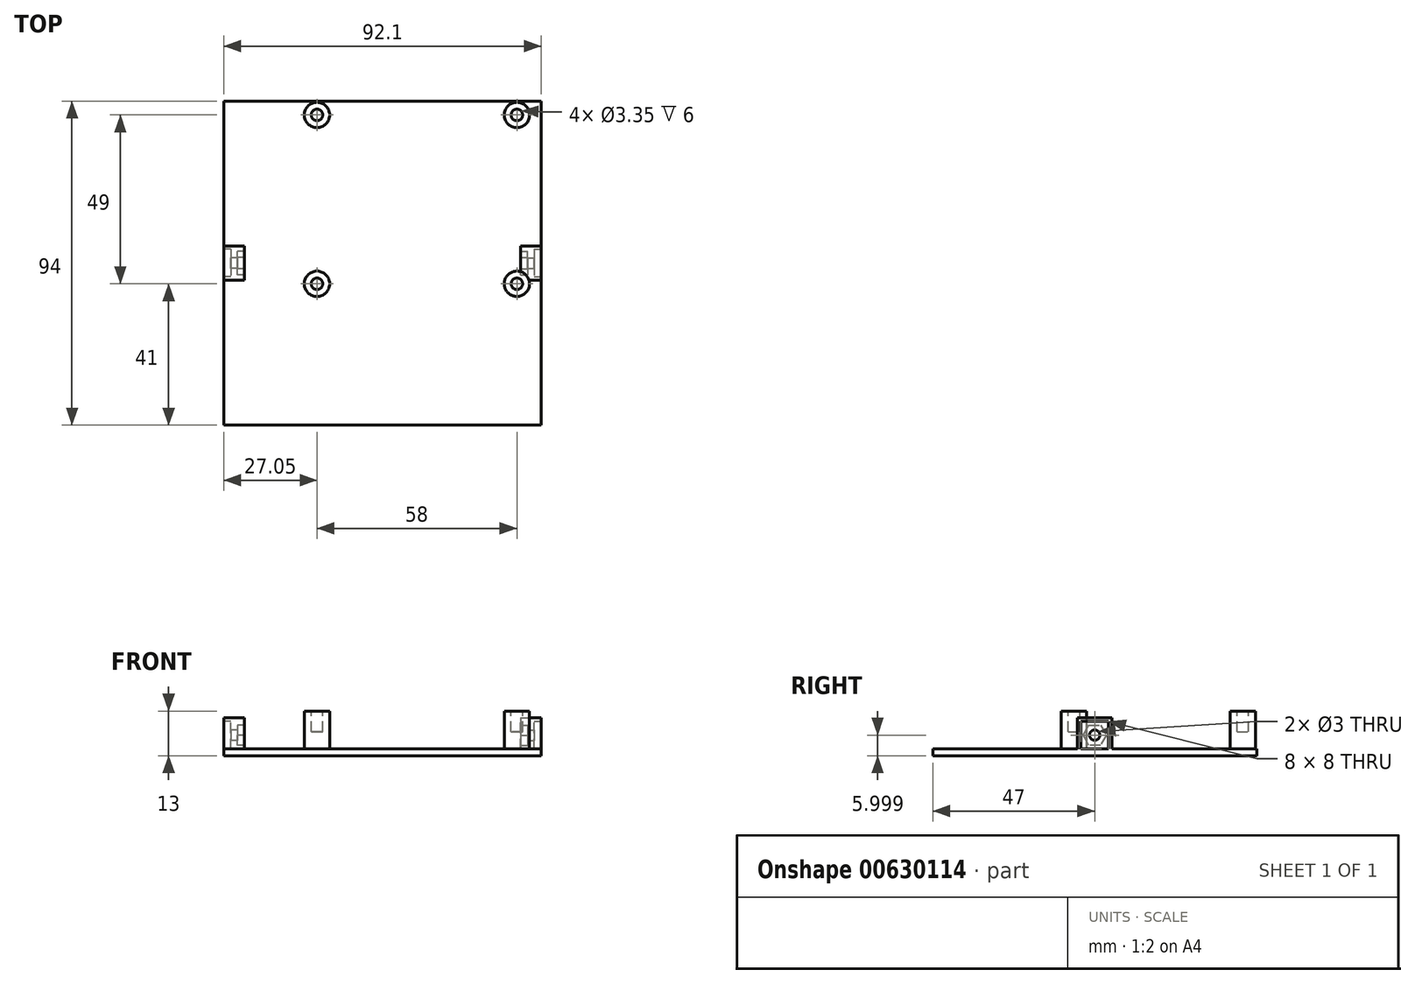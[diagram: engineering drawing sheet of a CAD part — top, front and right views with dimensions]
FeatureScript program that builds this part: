
annotation { "Feature Type Name" : "Feature", "Feature Type Description" : "" }
export const myFeature = defineFeature(function(context is Context, id is Id, definition is map)
    precondition{}
    {
        {
            var Q0;
            Q0=qCreatedBy(makeId("Right.planeOp"),FACE);
            var sketch = newSketch(context, id + "F0", { "sketchPlane" : qUnion([Q0])});
            skLineSegment(sketch, "E0.7", {"start": v(47, 6.17) * mm, "end": v(-47, 6.17) * mm});
            skLineSegment(sketch, "E1", {"start": v(47, 4.17) * mm, "end": v(-47, 4.17) * mm});
            skLineSegment(sketch, "E2", {"start": v(47, 6.17) * mm, "end": v(47, 4.17) * mm});
            skLineSegment(sketch, "E3", {"start": v(-47, 6.17) * mm, "end": v(-47, 4.17) * mm});
            skSolve(sketch);
        }
        {
            var Q0;
            Q0 = qSketchRegion(id + "F0", true);
            extrude(context, id + "F1", {"entities" : qUnion([Q0]), "depth" : 92.1 * mm, "offsetDistance" : 25 * mm, "symmetric" : true});
        }
        {
            var Q0;
            Q0=makeQuery(id+"F1.opExtrude","CAP_FACE",FACE,{"disambiguationData":[OSD([sQuery(id+"F0.wireOp",EDGE,"E0.7"),sQuery(id+"F0.wireOp",EDGE,"E1"),sQuery(id+"F0.wireOp",EDGE,"E2"),sQuery(id+"F0.wireOp",EDGE,"E3")])],"isStart":true});
            var sketch = newSketch(context, id + "F2", { "sketchPlane" : qUnion([Q0])});
            skPoint(sketch, "E4", {"position": v(0, 4.17) * mm});
            skLineSegment(sketch, "E5", {"start": v(0, 4.17) * mm, "end": v(0, 7.17) * mm, "construction": true});
            skLineSegment(sketch, "E6", {"start": v(0, 7.17) * mm, "end": v(0, 13.17) * mm, "construction": true});
            skPoint(sketch, "E7", {"position": v(0, 10.17) * mm});
            skCircle(sketch, "E8", {"center": v(0, 10.17) * mm, "radius": 1.5 * mm});
            skCircle(sketch, "E9", {"center": v(0, 10.17) * mm, "radius": 2.75 * mm, "construction": true});
            skLineSegment(sketch, "E10.bottom", {"start": v(-3, 7.17) * mm, "end": v(-3, 13.17) * mm, "construction": true});
            skLineSegment(sketch, "E10.top", {"start": v(3, 7.17) * mm, "end": v(3, 13.17) * mm, "construction": true});
            skLineSegment(sketch, "E10.left", {"start": v(-3, 7.17) * mm, "end": v(3, 7.17) * mm, "construction": true});
            skLineSegment(sketch, "E10.right", {"start": v(-3, 13.17) * mm, "end": v(3, 13.17) * mm, "construction": true});
            skLineSegment(sketch, "E11.bottom", {"start": v(-4, 6.17) * mm, "end": v(-4, 14.17) * mm});
            skLineSegment(sketch, "E11.top", {"start": v(4, 6.17) * mm, "end": v(4, 14.17) * mm});
            skLineSegment(sketch, "E11.left", {"start": v(-4, 6.17) * mm, "end": v(4, 6.17) * mm});
            skLineSegment(sketch, "E11.right", {"start": v(-4, 14.17) * mm, "end": v(4, 14.17) * mm});
            skLineSegment(sketch, "E12.bottom", {"start": v(-5, 5.17) * mm, "end": v(-5, 15.17) * mm});
            skLineSegment(sketch, "E12.top", {"start": v(5, 5.17) * mm, "end": v(5, 15.17) * mm});
            skLineSegment(sketch, "E12.left", {"start": v(-5, 5.17) * mm, "end": v(5, 5.17) * mm, "construction": true});
            skLineSegment(sketch, "E12.right", {"start": v(-5, 15.17) * mm, "end": v(5, 15.17) * mm});
            skSolve(sketch);
        }
        {
            var Q0;
            {var subQ6=sQuery(id+"F2.wireOp",EDGE,"E11.bottom");Q0=makeQuery(id+"F2.imprint","IMPRINT",FACE,{"disambiguationData":[TD([[makeQuery(id+"F2.imprint","IMPRINT",EDGE,{"derivedFrom":subQ6}),1.0]])]});}
            var Q1;
            Q1=makeQuery(id+"F2.imprint","IMPRINT",FACE,{"disambiguationData":[TD([[makeQuery(id+"F2.imprint","IMPRINT",EDGE,{"derivedFrom":sQuery(id+"F2.wireOp",EDGE,"E8")}),-1.0]])]});
            extrude(context, id + "F3", {"entities" : qUnion([Q0, Q1]), "operationType" : NewBodyOperationType.ADD, "oppositeDirection" : true, "depth" : 4 * mm, "offsetDistance" : 25 * mm});
        }
        {
            var Q0;
            Q0=makeQuery(id+"F2.imprint","IMPRINT",FACE,{"disambiguationData":[TD([[makeQuery(id+"F2.imprint","IMPRINT",EDGE,{"derivedFrom":sQuery(id+"F2.wireOp",EDGE,"E8")}),-1.0]])]});
            extrude(context, id + "F4", {"entities" : qUnion([Q0]), "operationType" : NewBodyOperationType.REMOVE, "oppositeDirection" : true, "depth" : 2 * mm, "offsetDistance" : 25 * mm});
        }
        {
            var Q0;
            Q0=makeQuery(id+"F3.opExtrude","CAP_FACE",FACE,{"disambiguationData":[OSD([sQuery(id+"F0.wireOp",EDGE,"E0.7"),sQuery(id+"F2.wireOp",EDGE,"E8"),sQuery(id+"F2.wireOp",EDGE,"E11.left"),sQuery(id+"F2.wireOp",EDGE,"E12.bottom"),sQuery(id+"F2.wireOp",EDGE,"E12.top"),sQuery(id+"F2.wireOp",EDGE,"E12.right")])],"isStart":false});
            var sketch = newSketch(context, id + "F5", { "sketchPlane" : qUnion([Q0])});
            skCircle(sketch, "E13.cCircle", {"center": v(0, 10.17) * mm, "radius": 2.92 * mm, "construction": true});
            skLineSegment(sketch, "E13.0", {"start": v(3.38, 10.17) * mm, "end": v(1.69, 7.25) * mm});
            skLineSegment(sketch, "E13.1", {"start": v(1.69, 7.25) * mm, "end": v(-1.69, 7.25) * mm});
            skLineSegment(sketch, "E13.2", {"start": v(-1.69, 7.25) * mm, "end": v(-3.37, 10.17) * mm});
            skLineSegment(sketch, "E13.3", {"start": v(-3.37, 10.17) * mm, "end": v(-1.69, 13.1) * mm});
            skLineSegment(sketch, "E13.4", {"start": v(-1.69, 13.1) * mm, "end": v(1.69, 13.1) * mm});
            skLineSegment(sketch, "E13.5", {"start": v(1.69, 13.1) * mm, "end": v(3.38, 10.17) * mm});
            skPoint(sketch, "E13.0.midPoint", {"position": v(2.53, 8.7) * mm});
            skLineSegment(sketch, "E14.bottom", {"start": v(-5, 15.17) * mm, "end": v(5, 15.17) * mm});
            skLineSegment(sketch, "E14.top", {"start": v(-5, 6.17) * mm, "end": v(5, 6.17) * mm});
            skLineSegment(sketch, "E14.left", {"start": v(-5, 15.17) * mm, "end": v(-5, 6.17) * mm});
            skLineSegment(sketch, "E14.right", {"start": v(5, 15.17) * mm, "end": v(5, 6.17) * mm});
            skSolve(sketch);
        }
        {
            var Q0;
            Q0=makeQuery(id+"F5.imprint","IMPRINT",FACE,{"disambiguationData":[TD([[makeQuery(id+"F5.imprint","IMPRINT",EDGE,{"derivedFrom":sQuery(id+"F5.wireOp",EDGE,"E13.0")}),1.0]])]});
            extrude(context, id + "F6", {"entities" : qUnion([Q0]), "operationType" : NewBodyOperationType.ADD, "depth" : 2 * mm, "offsetDistance" : 25 * mm});
        }
        {
            var Q0;
            Q0=makeQuery(id+"F1.opExtrude","SWEPT_BODY",BODY,{"disambiguationData":[OSD([sQuery(id+"F0.wireOp",EDGE,"E0.7"),sQuery(id+"F0.wireOp",EDGE,"E1"),sQuery(id+"F0.wireOp",EDGE,"E2"),sQuery(id+"F0.wireOp",EDGE,"E3")])]});
            var Q1;
            Q1=qCreatedBy(makeId("Right.planeOp"),FACE);
            mirror(context, id + "F7", {"entities" : qUnion([Q0]), "mirrorPlane" : qUnion([Q1])});
        }
        {
            var Q0;
            {var subQ10=sQuery(id+"F0.wireOp",EDGE,"E2");var subQ12=sQuery(id+"F0.wireOp",EDGE,"E0.7");Q0=makeQuery(id+"FgA4i82gOfAXOqg_2.opBoolean","SPLIT",FACE,{"disambiguationData":[TD([makeQuery(id+"F1.opExtrude","SWEPT_FACE",FACE,{"disambiguationData":[OSD([subQ10])]})])],"derivedFrom":makeQuery(id+"F1.opExtrude","SWEPT_FACE",FACE,{"disambiguationData":[OSD([subQ12])]})});}
            var sketch = newSketch(context, id + "F8", { "sketchPlane" : qUnion([Q0])});
            skLineSegment(sketch, "E15.bottom", {"start": v(42.5, 46.5) * mm, "end": v(-42.5, 46.5) * mm});
            skLineSegment(sketch, "E15.top", {"start": v(42.5, -9.5) * mm, "end": v(-42.5, -9.5) * mm});
            skLineSegment(sketch, "E15.left", {"start": v(42.5, 46.5) * mm, "end": v(42.5, -9.5) * mm});
            skLineSegment(sketch, "E15.right", {"start": v(-42.5, 46.5) * mm, "end": v(-42.5, -9.5) * mm});
            skCircle(sketch, "E16", {"center": v(39, -6) * mm, "radius": 1.38 * mm});
            skCircle(sketch, "E17", {"center": v(-19, -6) * mm, "radius": 1.38 * mm});
            skCircle(sketch, "E18", {"center": v(-19, 43) * mm, "radius": 1.38 * mm});
            skCircle(sketch, "E19", {"center": v(39, 43) * mm, "radius": 1.37 * mm});
            skLineSegment(sketch, "E20.bottom", {"start": v(35, -8.5) * mm, "end": v(-15, -8.5) * mm, "construction": true});
            skLineSegment(sketch, "E20.top", {"start": v(35, -3.5) * mm, "end": v(-15, -3.5) * mm, "construction": true});
            skLineSegment(sketch, "E20.left", {"start": v(35, -8.5) * mm, "end": v(35, -3.5) * mm, "construction": true});
            skLineSegment(sketch, "E20.right", {"start": v(-15, -8.5) * mm, "end": v(-15, -3.5) * mm, "construction": true});
            skLineSegment(sketch, "E21", {"start": v(10, -8.5) * mm, "end": v(10, -3.5) * mm, "construction": true});
            skLineSegment(sketch, "E22", {"start": v(35, -6) * mm, "end": v(-15, -6) * mm, "construction": true});
            skLineSegment(sketch, "E23.bottom", {"start": v(34.05, -7.55) * mm, "end": v(33.45, -7.55) * mm});
            skLineSegment(sketch, "E23.top", {"start": v(34.05, -6.95) * mm, "end": v(33.45, -6.95) * mm});
            skLineSegment(sketch, "E23.left", {"start": v(34.05, -7.55) * mm, "end": v(34.05, -6.95) * mm});
            skLineSegment(sketch, "E23.right", {"start": v(33.45, -7.55) * mm, "end": v(33.45, -6.95) * mm});
            skLineSegment(sketch, "E24", {"start": v(32.5, -8.5) * mm, "end": v(32.5, -3.5) * mm, "construction": true});
            skLineSegment(sketch, "E25.1.0.0", {"start": v(31.55, -6.95) * mm, "end": v(30.95, -6.95) * mm});
            skLineSegment(sketch, "E25.1.0.1", {"start": v(31.55, -7.55) * mm, "end": v(30.95, -7.55) * mm});
            skLineSegment(sketch, "E25.1.0.2", {"start": v(30.95, -7.55) * mm, "end": v(30.95, -6.95) * mm});
            skLineSegment(sketch, "E25.1.0.3", {"start": v(31.55, -7.55) * mm, "end": v(31.55, -6.95) * mm});
            skLineSegment(sketch, "E25.2.0.0", {"start": v(29.05, -6.95) * mm, "end": v(28.45, -6.95) * mm});
            skLineSegment(sketch, "E25.2.0.1", {"start": v(29.05, -7.55) * mm, "end": v(28.45, -7.55) * mm});
            skLineSegment(sketch, "E25.2.0.2", {"start": v(28.45, -7.55) * mm, "end": v(28.45, -6.95) * mm});
            skLineSegment(sketch, "E25.2.0.3", {"start": v(29.05, -7.55) * mm, "end": v(29.05, -6.95) * mm});
            skLineSegment(sketch, "E25.3.0.0", {"start": v(26.55, -6.95) * mm, "end": v(25.95, -6.95) * mm});
            skLineSegment(sketch, "E25.3.0.1", {"start": v(26.55, -7.55) * mm, "end": v(25.95, -7.55) * mm});
            skLineSegment(sketch, "E25.3.0.2", {"start": v(25.95, -7.55) * mm, "end": v(25.95, -6.95) * mm});
            skLineSegment(sketch, "E25.3.0.3", {"start": v(26.55, -7.55) * mm, "end": v(26.55, -6.95) * mm});
            skLineSegment(sketch, "E25.4.0.0", {"start": v(24.05, -6.95) * mm, "end": v(23.45, -6.95) * mm});
            skLineSegment(sketch, "E25.4.0.1", {"start": v(24.05, -7.55) * mm, "end": v(23.45, -7.55) * mm});
            skLineSegment(sketch, "E25.4.0.2", {"start": v(23.45, -7.55) * mm, "end": v(23.45, -6.95) * mm});
            skLineSegment(sketch, "E25.4.0.3", {"start": v(24.05, -7.55) * mm, "end": v(24.05, -6.95) * mm});
            skLineSegment(sketch, "E25.5.0.0", {"start": v(21.55, -6.95) * mm, "end": v(20.95, -6.95) * mm});
            skLineSegment(sketch, "E25.5.0.1", {"start": v(21.55, -7.55) * mm, "end": v(20.95, -7.55) * mm});
            skLineSegment(sketch, "E25.5.0.2", {"start": v(20.95, -7.55) * mm, "end": v(20.95, -6.95) * mm});
            skLineSegment(sketch, "E25.5.0.3", {"start": v(21.55, -7.55) * mm, "end": v(21.55, -6.95) * mm});
            skLineSegment(sketch, "E25.6.0.0", {"start": v(19.05, -6.95) * mm, "end": v(18.45, -6.95) * mm});
            skLineSegment(sketch, "E25.6.0.1", {"start": v(19.05, -7.55) * mm, "end": v(18.45, -7.55) * mm});
            skLineSegment(sketch, "E25.6.0.2", {"start": v(18.45, -7.55) * mm, "end": v(18.45, -6.95) * mm});
            skLineSegment(sketch, "E25.6.0.3", {"start": v(19.05, -7.55) * mm, "end": v(19.05, -6.95) * mm});
            skLineSegment(sketch, "E25.7.0.0", {"start": v(16.55, -6.95) * mm, "end": v(15.95, -6.95) * mm});
            skLineSegment(sketch, "E25.7.0.1", {"start": v(16.55, -7.55) * mm, "end": v(15.95, -7.55) * mm});
            skLineSegment(sketch, "E25.7.0.2", {"start": v(15.95, -7.55) * mm, "end": v(15.95, -6.95) * mm});
            skLineSegment(sketch, "E25.7.0.3", {"start": v(16.55, -7.55) * mm, "end": v(16.55, -6.95) * mm});
            skLineSegment(sketch, "E25.8.0.0", {"start": v(14.05, -6.95) * mm, "end": v(13.45, -6.95) * mm});
            skLineSegment(sketch, "E25.8.0.1", {"start": v(14.05, -7.55) * mm, "end": v(13.45, -7.55) * mm});
            skLineSegment(sketch, "E25.8.0.2", {"start": v(13.45, -7.55) * mm, "end": v(13.45, -6.95) * mm});
            skLineSegment(sketch, "E25.8.0.3", {"start": v(14.05, -7.55) * mm, "end": v(14.05, -6.95) * mm});
            skLineSegment(sketch, "E25.9.0.0", {"start": v(11.55, -6.95) * mm, "end": v(10.95, -6.95) * mm});
            skLineSegment(sketch, "E25.9.0.1", {"start": v(11.55, -7.55) * mm, "end": v(10.95, -7.55) * mm});
            skLineSegment(sketch, "E25.9.0.2", {"start": v(10.95, -7.55) * mm, "end": v(10.95, -6.95) * mm});
            skLineSegment(sketch, "E25.9.0.3", {"start": v(11.55, -7.55) * mm, "end": v(11.55, -6.95) * mm});
            skLineSegment(sketch, "E25.direction1", {"start": v(34.05, -6.95) * mm, "end": v(31.55, -6.95) * mm, "construction": true});
            skLineSegment(sketch, "E26.MirrorCS", {"start": v(14.05, -5.05) * mm, "end": v(13.45, -5.05) * mm});
            skLineSegment(sketch, "E27.MirrorCS", {"start": v(14.05, -4.45) * mm, "end": v(13.45, -4.45) * mm});
            skLineSegment(sketch, "E28.MirrorCS", {"start": v(11.55, -4.45) * mm, "end": v(10.95, -4.45) * mm});
            skLineSegment(sketch, "E29.MirrorCS", {"start": v(31.55, -4.45) * mm, "end": v(30.95, -4.45) * mm});
            skLineSegment(sketch, "E30.MirrorCS", {"start": v(31.55, -5.05) * mm, "end": v(30.95, -5.05) * mm});
            skLineSegment(sketch, "E31.MirrorCS", {"start": v(11.55, -5.05) * mm, "end": v(10.95, -5.05) * mm});
            skLineSegment(sketch, "E32.MirrorCS", {"start": v(34.05, -4.45) * mm, "end": v(33.45, -4.45) * mm});
            skLineSegment(sketch, "E33.MirrorCS", {"start": v(34.05, -5.05) * mm, "end": v(33.45, -5.05) * mm});
            skLineSegment(sketch, "E34.MirrorCS", {"start": v(33.45, -4.45) * mm, "end": v(33.45, -5.05) * mm});
            skLineSegment(sketch, "E35.MirrorCS", {"start": v(24.05, -4.45) * mm, "end": v(24.05, -5.05) * mm});
            skLineSegment(sketch, "E36.MirrorCS", {"start": v(14.05, -4.45) * mm, "end": v(14.05, -5.05) * mm});
            skLineSegment(sketch, "E37.MirrorCS", {"start": v(21.55, -4.45) * mm, "end": v(21.55, -5.05) * mm});
            skLineSegment(sketch, "E38.MirrorCS", {"start": v(24.05, -5.05) * mm, "end": v(23.45, -5.05) * mm});
            skLineSegment(sketch, "E39.MirrorCS", {"start": v(11.55, -4.45) * mm, "end": v(11.55, -5.05) * mm});
            skLineSegment(sketch, "E40.MirrorCS", {"start": v(31.55, -4.45) * mm, "end": v(31.55, -5.05) * mm});
            skLineSegment(sketch, "E41.MirrorCS", {"start": v(28.45, -4.45) * mm, "end": v(28.45, -5.05) * mm});
            skLineSegment(sketch, "E42.MirrorCS", {"start": v(18.45, -4.45) * mm, "end": v(18.45, -5.05) * mm});
            skLineSegment(sketch, "E43.MirrorCS", {"start": v(23.45, -4.45) * mm, "end": v(23.45, -5.05) * mm});
            skLineSegment(sketch, "E44.MirrorCS", {"start": v(13.45, -4.45) * mm, "end": v(13.45, -5.05) * mm});
            skLineSegment(sketch, "E45.MirrorCS", {"start": v(20.95, -4.45) * mm, "end": v(20.95, -5.05) * mm});
            skLineSegment(sketch, "E46.MirrorCS", {"start": v(26.55, -4.45) * mm, "end": v(26.55, -5.05) * mm});
            skLineSegment(sketch, "E47.MirrorCS", {"start": v(10.95, -4.45) * mm, "end": v(10.95, -5.05) * mm});
            skLineSegment(sketch, "E48.MirrorCS", {"start": v(16.55, -4.45) * mm, "end": v(16.55, -5.05) * mm});
            skLineSegment(sketch, "E49.MirrorCS", {"start": v(30.95, -4.45) * mm, "end": v(30.95, -5.05) * mm});
            skLineSegment(sketch, "E50.MirrorCS", {"start": v(29.05, -4.45) * mm, "end": v(28.45, -4.45) * mm});
            skLineSegment(sketch, "E51.MirrorCS", {"start": v(19.05, -4.45) * mm, "end": v(18.45, -4.45) * mm});
            skLineSegment(sketch, "E52.MirrorCS", {"start": v(26.55, -4.45) * mm, "end": v(25.95, -4.45) * mm});
            skLineSegment(sketch, "E53.MirrorCS", {"start": v(16.55, -4.45) * mm, "end": v(15.95, -4.45) * mm});
            skLineSegment(sketch, "E54.MirrorCS", {"start": v(24.05, -4.45) * mm, "end": v(23.45, -4.45) * mm});
            skLineSegment(sketch, "E55.MirrorCS", {"start": v(34.05, -4.45) * mm, "end": v(34.05, -5.05) * mm});
            skLineSegment(sketch, "E56.MirrorCS", {"start": v(21.55, -4.45) * mm, "end": v(20.95, -4.45) * mm});
            skLineSegment(sketch, "E57.MirrorCS", {"start": v(25.95, -4.45) * mm, "end": v(25.95, -5.05) * mm});
            skLineSegment(sketch, "E58.MirrorCS", {"start": v(15.95, -4.45) * mm, "end": v(15.95, -5.05) * mm});
            skLineSegment(sketch, "E59.MirrorCS", {"start": v(29.05, -5.05) * mm, "end": v(28.45, -5.05) * mm});
            skLineSegment(sketch, "E60.MirrorCS", {"start": v(19.05, -5.05) * mm, "end": v(18.45, -5.05) * mm});
            skLineSegment(sketch, "E61.MirrorCS", {"start": v(34.05, -5.05) * mm, "end": v(31.55, -5.05) * mm, "construction": true});
            skLineSegment(sketch, "E62.MirrorCS", {"start": v(26.55, -5.05) * mm, "end": v(25.95, -5.05) * mm});
            skLineSegment(sketch, "E63.MirrorCS", {"start": v(16.55, -5.05) * mm, "end": v(15.95, -5.05) * mm});
            skLineSegment(sketch, "E64.MirrorCS", {"start": v(29.05, -4.45) * mm, "end": v(29.05, -5.05) * mm});
            skLineSegment(sketch, "E65.MirrorCS", {"start": v(19.05, -4.45) * mm, "end": v(19.05, -5.05) * mm});
            skLineSegment(sketch, "E66.MirrorCS", {"start": v(21.55, -5.05) * mm, "end": v(20.95, -5.05) * mm});
            skLineSegment(sketch, "E67.MirrorCS", {"start": v(-6.55, -4.45) * mm, "end": v(-5.95, -4.45) * mm});
            skLineSegment(sketch, "E68.MirrorCS", {"start": v(0.95, -4.45) * mm, "end": v(1.55, -4.45) * mm});
            skLineSegment(sketch, "E69.MirrorCS", {"start": v(0.95, -7.55) * mm, "end": v(1.55, -7.55) * mm});
            skLineSegment(sketch, "E70.MirrorCS", {"start": v(-4.05, -7.55) * mm, "end": v(-3.45, -7.55) * mm});
            skLineSegment(sketch, "E71.MirrorCS", {"start": v(0.95, -6.95) * mm, "end": v(1.55, -6.95) * mm});
            skLineSegment(sketch, "E72.MirrorCS", {"start": v(-1.55, -5.05) * mm, "end": v(-0.95, -5.05) * mm});
            skLineSegment(sketch, "E73.MirrorCS", {"start": v(0.95, -5.05) * mm, "end": v(1.55, -5.05) * mm});
            skLineSegment(sketch, "E74.MirrorCS", {"start": v(-6.55, -7.55) * mm, "end": v(-5.95, -7.55) * mm});
            skLineSegment(sketch, "E75.MirrorCS", {"start": v(-6.55, -5.05) * mm, "end": v(-5.95, -5.05) * mm});
            skLineSegment(sketch, "E76.MirrorCS", {"start": v(-1.55, -6.95) * mm, "end": v(-0.95, -6.95) * mm});
            skLineSegment(sketch, "E77.MirrorCS", {"start": v(-6.55, -6.95) * mm, "end": v(-5.95, -6.95) * mm});
            skLineSegment(sketch, "E78.MirrorCS", {"start": v(-4.05, -4.45) * mm, "end": v(-3.45, -4.45) * mm});
            skLineSegment(sketch, "E79.MirrorCS", {"start": v(-4.05, -5.05) * mm, "end": v(-3.45, -5.05) * mm});
            skLineSegment(sketch, "E80.MirrorCS", {"start": v(-1.55, -7.55) * mm, "end": v(-0.95, -7.55) * mm});
            skLineSegment(sketch, "E81.MirrorCS", {"start": v(-1.55, -4.45) * mm, "end": v(-0.95, -4.45) * mm});
            skLineSegment(sketch, "E82.MirrorCS", {"start": v(-4.05, -6.95) * mm, "end": v(-3.45, -6.95) * mm});
            skLineSegment(sketch, "E83.MirrorCS", {"start": v(-13.45, -7.55) * mm, "end": v(-13.45, -6.95) * mm});
            skLineSegment(sketch, "E84.MirrorCS", {"start": v(-14.05, -6.95) * mm, "end": v(-13.45, -6.95) * mm});
            skLineSegment(sketch, "E85.MirrorCS", {"start": v(-14.05, -5.05) * mm, "end": v(-13.45, -5.05) * mm});
            skLineSegment(sketch, "E86.MirrorCS", {"start": v(-4.05, -7.55) * mm, "end": v(-4.05, -6.95) * mm});
            skLineSegment(sketch, "E87.MirrorCS", {"start": v(5.95, -7.55) * mm, "end": v(5.95, -6.95) * mm});
            skLineSegment(sketch, "E88.MirrorCS", {"start": v(5.95, -4.45) * mm, "end": v(5.95, -5.05) * mm});
            skLineSegment(sketch, "E89.MirrorCS", {"start": v(-3.45, -4.45) * mm, "end": v(-3.45, -5.05) * mm});
            skLineSegment(sketch, "E90.MirrorCS", {"start": v(-9.05, -5.05) * mm, "end": v(-8.45, -5.05) * mm});
            skLineSegment(sketch, "E91.MirrorCS", {"start": v(-8.45, -7.55) * mm, "end": v(-8.45, -6.95) * mm});
            skLineSegment(sketch, "E92.MirrorCS", {"start": v(1.55, -7.55) * mm, "end": v(1.55, -6.95) * mm});
            skLineSegment(sketch, "E93.MirrorCS", {"start": v(5.95, -4.45) * mm, "end": v(6.55, -4.45) * mm});
            skLineSegment(sketch, "E94.MirrorCS", {"start": v(-3.45, -7.55) * mm, "end": v(-3.45, -6.95) * mm});
            skLineSegment(sketch, "E95.MirrorCS", {"start": v(6.55, -7.55) * mm, "end": v(6.55, -6.95) * mm});
            skLineSegment(sketch, "E96.MirrorCS", {"start": v(-4.05, -4.45) * mm, "end": v(-4.05, -5.05) * mm});
            skLineSegment(sketch, "E97.MirrorCS", {"start": v(1.55, -4.45) * mm, "end": v(1.55, -5.05) * mm});
            skLineSegment(sketch, "E98.MirrorCS", {"start": v(4.05, -4.45) * mm, "end": v(4.05, -5.05) * mm});
            skLineSegment(sketch, "E99.MirrorCS", {"start": v(-9.05, -7.55) * mm, "end": v(-8.45, -7.55) * mm});
            skLineSegment(sketch, "E100.MirrorCS", {"start": v(5.95, -5.05) * mm, "end": v(6.55, -5.05) * mm});
            skLineSegment(sketch, "E101.MirrorCS", {"start": v(5.95, -7.55) * mm, "end": v(6.55, -7.55) * mm});
            skLineSegment(sketch, "E102.MirrorCS", {"start": v(-13.45, -4.45) * mm, "end": v(-13.45, -5.05) * mm});
            skLineSegment(sketch, "E103.MirrorCS", {"start": v(-9.05, -4.45) * mm, "end": v(-8.45, -4.45) * mm});
            skLineSegment(sketch, "E104.MirrorCS", {"start": v(-14.05, -7.55) * mm, "end": v(-14.05, -6.95) * mm});
            skLineSegment(sketch, "E105.MirrorCS", {"start": v(-8.45, -4.45) * mm, "end": v(-8.45, -5.05) * mm});
            skLineSegment(sketch, "E106.MirrorCS", {"start": v(-5.95, -4.45) * mm, "end": v(-5.95, -5.05) * mm});
            skLineSegment(sketch, "E107.MirrorCS", {"start": v(-9.05, -6.95) * mm, "end": v(-8.45, -6.95) * mm});
            skLineSegment(sketch, "E108.MirrorCS", {"start": v(-14.05, -6.95) * mm, "end": v(-11.55, -6.95) * mm, "construction": true});
            skLineSegment(sketch, "E109.MirrorCS", {"start": v(8.45, -4.45) * mm, "end": v(9.05, -4.45) * mm});
            skLineSegment(sketch, "E110.MirrorCS", {"start": v(0.95, -7.55) * mm, "end": v(0.95, -6.95) * mm});
            skLineSegment(sketch, "E111.MirrorCS", {"start": v(-9.05, -7.55) * mm, "end": v(-9.05, -6.95) * mm});
            skLineSegment(sketch, "E112.MirrorCS", {"start": v(6.55, -4.45) * mm, "end": v(6.55, -5.05) * mm});
            skLineSegment(sketch, "E113.MirrorCS", {"start": v(3.45, -7.55) * mm, "end": v(4.05, -7.55) * mm});
            skLineSegment(sketch, "E114.MirrorCS", {"start": v(-11.55, -5.05) * mm, "end": v(-10.95, -5.05) * mm});
            skLineSegment(sketch, "E115.MirrorCS", {"start": v(-6.55, -4.45) * mm, "end": v(-6.55, -5.05) * mm});
            skLineSegment(sketch, "E116.MirrorCS", {"start": v(-10.95, -7.55) * mm, "end": v(-10.95, -6.95) * mm});
            skLineSegment(sketch, "E117.MirrorCS", {"start": v(-11.55, -6.95) * mm, "end": v(-10.95, -6.95) * mm});
            skLineSegment(sketch, "E118.MirrorCS", {"start": v(3.45, -4.45) * mm, "end": v(4.05, -4.45) * mm});
            skLineSegment(sketch, "E119.MirrorCS", {"start": v(-1.55, -4.45) * mm, "end": v(-1.55, -5.05) * mm});
            skLineSegment(sketch, "E120.MirrorCS", {"start": v(8.45, -6.95) * mm, "end": v(9.05, -6.95) * mm});
            skLineSegment(sketch, "E121.MirrorCS", {"start": v(3.45, -4.45) * mm, "end": v(3.45, -5.05) * mm});
            skLineSegment(sketch, "E122.MirrorCS", {"start": v(-14.05, -4.45) * mm, "end": v(-14.05, -5.05) * mm});
            skLineSegment(sketch, "E123.MirrorCS", {"start": v(9.05, -7.55) * mm, "end": v(9.05, -6.95) * mm});
            skLineSegment(sketch, "E124.MirrorCS", {"start": v(-14.05, -4.45) * mm, "end": v(-13.45, -4.45) * mm});
            skLineSegment(sketch, "E125.MirrorCS", {"start": v(8.45, -4.45) * mm, "end": v(8.45, -5.05) * mm});
            skLineSegment(sketch, "E126.MirrorCS", {"start": v(3.45, -7.55) * mm, "end": v(3.45, -6.95) * mm});
            skLineSegment(sketch, "E127.MirrorCS", {"start": v(-6.55, -7.55) * mm, "end": v(-6.55, -6.95) * mm});
            skLineSegment(sketch, "E128.MirrorCS", {"start": v(-0.95, -7.55) * mm, "end": v(-0.95, -6.95) * mm});
            skLineSegment(sketch, "E129.MirrorCS", {"start": v(-9.05, -4.45) * mm, "end": v(-9.05, -5.05) * mm});
            skLineSegment(sketch, "E130.MirrorCS", {"start": v(-11.55, -4.45) * mm, "end": v(-10.95, -4.45) * mm});
            skLineSegment(sketch, "E131.MirrorCS", {"start": v(3.45, -6.95) * mm, "end": v(4.05, -6.95) * mm});
            skLineSegment(sketch, "E132.MirrorCS", {"start": v(-14.05, -5.05) * mm, "end": v(-11.55, -5.05) * mm, "construction": true});
            skLineSegment(sketch, "E133.MirrorCS", {"start": v(-0.95, -4.45) * mm, "end": v(-0.95, -5.05) * mm});
            skLineSegment(sketch, "E134.MirrorCS", {"start": v(-11.55, -7.55) * mm, "end": v(-10.95, -7.55) * mm});
            skLineSegment(sketch, "E135.MirrorCS", {"start": v(9.05, -4.45) * mm, "end": v(9.05, -5.05) * mm});
            skLineSegment(sketch, "E136.MirrorCS", {"start": v(8.45, -5.05) * mm, "end": v(9.05, -5.05) * mm});
            skLineSegment(sketch, "E137.MirrorCS", {"start": v(4.05, -7.55) * mm, "end": v(4.05, -6.95) * mm});
            skLineSegment(sketch, "E138.MirrorCS", {"start": v(8.45, -7.55) * mm, "end": v(9.05, -7.55) * mm});
            skLineSegment(sketch, "E139.MirrorCS", {"start": v(3.45, -5.05) * mm, "end": v(4.05, -5.05) * mm});
            skLineSegment(sketch, "E140.MirrorCS", {"start": v(-14.05, -7.55) * mm, "end": v(-13.45, -7.55) * mm});
            skLineSegment(sketch, "E141.MirrorCS", {"start": v(-11.55, -7.55) * mm, "end": v(-11.55, -6.95) * mm});
            skLineSegment(sketch, "E142.MirrorCS", {"start": v(-10.95, -4.45) * mm, "end": v(-10.95, -5.05) * mm});
            skLineSegment(sketch, "E143.MirrorCS", {"start": v(-5.95, -7.55) * mm, "end": v(-5.95, -6.95) * mm});
            skLineSegment(sketch, "E144.MirrorCS", {"start": v(-11.55, -4.45) * mm, "end": v(-11.55, -5.05) * mm});
            skLineSegment(sketch, "E145.MirrorCS", {"start": v(8.45, -7.55) * mm, "end": v(8.45, -6.95) * mm});
            skLineSegment(sketch, "E146.MirrorCS", {"start": v(5.95, -6.95) * mm, "end": v(6.55, -6.95) * mm});
            skLineSegment(sketch, "E147.MirrorCS", {"start": v(0.95, -4.45) * mm, "end": v(0.95, -5.05) * mm});
            skLineSegment(sketch, "E148.MirrorCS", {"start": v(-1.55, -7.55) * mm, "end": v(-1.55, -6.95) * mm});
            skLineSegment(sketch, "E149", {"start": v(42.5, 18.5) * mm, "end": v(-42.5, 18.5) * mm, "construction": true});
            skLineSegment(sketch, "E150.bottom", {"start": v(40.7, 12.5) * mm, "end": v(38.7, 12.5) * mm});
            skLineSegment(sketch, "E150.top", {"start": v(40.7, 13) * mm, "end": v(38.7, 13) * mm});
            skLineSegment(sketch, "E150.left", {"start": v(40.7, 12.5) * mm, "end": v(40.7, 13) * mm});
            skLineSegment(sketch, "E150.right", {"start": v(38.7, 12.5) * mm, "end": v(38.7, 13) * mm});
            skLineSegment(sketch, "E151.MirrorCS", {"start": v(40.7, 24.5) * mm, "end": v(38.7, 24.5) * mm});
            skLineSegment(sketch, "E152.MirrorCS", {"start": v(38.7, 24.5) * mm, "end": v(38.7, 24) * mm});
            skLineSegment(sketch, "E153.MirrorCS", {"start": v(40.7, 24) * mm, "end": v(38.7, 24) * mm});
            skLineSegment(sketch, "E154.MirrorCS", {"start": v(40.7, 24.5) * mm, "end": v(40.7, 24) * mm});
            skLineSegment(sketch, "E155.bottom", {"start": v(18, 38) * mm, "end": v(17.5, 38) * mm});
            skLineSegment(sketch, "E155.top", {"start": v(18, 44) * mm, "end": v(17.5, 44) * mm});
            skLineSegment(sketch, "E155.left", {"start": v(18, 38) * mm, "end": v(18, 44) * mm});
            skLineSegment(sketch, "E155.right", {"start": v(17.5, 38) * mm, "end": v(17.5, 44) * mm});
            skLineSegment(sketch, "E156", {"start": v(10.5, 46.5) * mm, "end": v(10.5, -9.5) * mm, "construction": true});
            skLineSegment(sketch, "E157.MirrorCS", {"start": v(3, 44) * mm, "end": v(3.5, 44) * mm});
            skLineSegment(sketch, "E158.MirrorCS", {"start": v(3, 38) * mm, "end": v(3.5, 38) * mm});
            skLineSegment(sketch, "E159.MirrorCS", {"start": v(3, 38) * mm, "end": v(3, 44) * mm});
            skLineSegment(sketch, "E160.MirrorCS", {"start": v(3.5, 38) * mm, "end": v(3.5, 44) * mm});
            skLineSegment(sketch, "E161.bottom", {"start": v(34.4, 43.5) * mm, "end": v(33.9, 43.5) * mm});
            skLineSegment(sketch, "E161.top", {"start": v(34.4, 45.5) * mm, "end": v(33.9, 45.5) * mm});
            skLineSegment(sketch, "E161.left", {"start": v(34.4, 43.5) * mm, "end": v(34.4, 45.5) * mm});
            skLineSegment(sketch, "E161.right", {"start": v(33.9, 43.5) * mm, "end": v(33.9, 45.5) * mm});
            skLineSegment(sketch, "E162", {"start": v(31.9, -9.5) * mm, "end": v(31.9, 46.5) * mm, "construction": true});
            skLineSegment(sketch, "E163.MirrorCS", {"start": v(29.4, 45.5) * mm, "end": v(29.9, 45.5) * mm});
            skLineSegment(sketch, "E164.MirrorCS", {"start": v(29.4, 43.5) * mm, "end": v(29.9, 43.5) * mm});
            skLineSegment(sketch, "E165.MirrorCS", {"start": v(29.4, 43.5) * mm, "end": v(29.4, 45.5) * mm});
            skLineSegment(sketch, "E166.MirrorCS", {"start": v(29.9, 43.5) * mm, "end": v(29.9, 45.5) * mm});
            skLineSegment(sketch, "E167", {"start": v(-11, 46.5) * mm, "end": v(-11, -9.5) * mm, "construction": true});
            skLineSegment(sketch, "E168.bottom", {"start": v(-7.5, 34) * mm, "end": v(-8, 34) * mm});
            skLineSegment(sketch, "E168.top", {"start": v(-7.5, 35) * mm, "end": v(-8, 35) * mm});
            skLineSegment(sketch, "E168.left", {"start": v(-7.5, 34) * mm, "end": v(-7.5, 35) * mm});
            skLineSegment(sketch, "E168.right", {"start": v(-8, 34) * mm, "end": v(-8, 35) * mm});
            skLineSegment(sketch, "E169.bottom", {"start": v(-7.5, 44) * mm, "end": v(-8, 44) * mm});
            skLineSegment(sketch, "E169.top", {"start": v(-7.5, 45) * mm, "end": v(-8, 45) * mm});
            skLineSegment(sketch, "E169.left", {"start": v(-7.5, 44) * mm, "end": v(-7.5, 45) * mm});
            skLineSegment(sketch, "E169.right", {"start": v(-8, 44) * mm, "end": v(-8, 45) * mm});
            skLineSegment(sketch, "E170.MirrorCS", {"start": v(-14.5, 35) * mm, "end": v(-14, 35) * mm});
            skLineSegment(sketch, "E171.MirrorCS", {"start": v(-14.5, 34) * mm, "end": v(-14, 34) * mm});
            skLineSegment(sketch, "E172.MirrorCS", {"start": v(-14.5, 45) * mm, "end": v(-14, 45) * mm});
            skLineSegment(sketch, "E173.MirrorCS", {"start": v(-14.5, 44) * mm, "end": v(-14, 44) * mm});
            skLineSegment(sketch, "E174.MirrorCS", {"start": v(-14, 44) * mm, "end": v(-14, 45) * mm});
            skLineSegment(sketch, "E175.MirrorCS", {"start": v(-14.5, 44) * mm, "end": v(-14.5, 45) * mm});
            skLineSegment(sketch, "E176.MirrorCS", {"start": v(-14.5, 34) * mm, "end": v(-14.5, 35) * mm});
            skLineSegment(sketch, "E177.MirrorCS", {"start": v(-14, 34) * mm, "end": v(-14, 35) * mm});
            skLineSegment(sketch, "E178", {"start": v(42.5, -0.5) * mm, "end": v(-42.5, -0.5) * mm, "construction": true});
            skLineSegment(sketch, "E179.bottom", {"start": v(-27, -7) * mm, "end": v(-28, -7) * mm});
            skLineSegment(sketch, "E179.top", {"start": v(-27, -6.5) * mm, "end": v(-28, -6.5) * mm});
            skLineSegment(sketch, "E179.left", {"start": v(-27, -7) * mm, "end": v(-27, -6.5) * mm});
            skLineSegment(sketch, "E179.right", {"start": v(-28, -7) * mm, "end": v(-28, -6.5) * mm});
            skLineSegment(sketch, "E180.bottom", {"start": v(-34, -7) * mm, "end": v(-35, -7) * mm});
            skLineSegment(sketch, "E180.top", {"start": v(-34, -6.5) * mm, "end": v(-35, -6.5) * mm});
            skLineSegment(sketch, "E180.left", {"start": v(-34, -7) * mm, "end": v(-34, -6.5) * mm});
            skLineSegment(sketch, "E180.right", {"start": v(-35, -7) * mm, "end": v(-35, -6.5) * mm});
            skLineSegment(sketch, "E181.MirrorCS", {"start": v(-27, 6) * mm, "end": v(-27, 5.5) * mm});
            skLineSegment(sketch, "E182.MirrorCS", {"start": v(-34, 6) * mm, "end": v(-34, 5.5) * mm});
            skLineSegment(sketch, "E183.MirrorCS", {"start": v(-35, 6) * mm, "end": v(-35, 5.5) * mm});
            skLineSegment(sketch, "E184.MirrorCS", {"start": v(-28, 6) * mm, "end": v(-28, 5.5) * mm});
            skLineSegment(sketch, "E185.MirrorCS", {"start": v(-27, 6) * mm, "end": v(-28, 6) * mm});
            skLineSegment(sketch, "E186.MirrorCS", {"start": v(-27, 5.5) * mm, "end": v(-28, 5.5) * mm});
            skLineSegment(sketch, "E187.MirrorCS", {"start": v(-34, 6) * mm, "end": v(-35, 6) * mm});
            skLineSegment(sketch, "E188.MirrorCS", {"start": v(-34, 5.5) * mm, "end": v(-35, 5.5) * mm});
            skLineSegment(sketch, "E189", {"start": v(42.5, 17.5) * mm, "end": v(-42.5, 17.5) * mm, "construction": true});
            skLineSegment(sketch, "E190.bottom", {"start": v(-27, 11.5) * mm, "end": v(-28, 11.5) * mm});
            skLineSegment(sketch, "E190.top", {"start": v(-27, 11) * mm, "end": v(-28, 11) * mm});
            skLineSegment(sketch, "E190.left", {"start": v(-27, 11.5) * mm, "end": v(-27, 11) * mm});
            skLineSegment(sketch, "E190.right", {"start": v(-28, 11.5) * mm, "end": v(-28, 11) * mm});
            skLineSegment(sketch, "E191.bottom", {"start": v(-34, 11.5) * mm, "end": v(-35, 11.5) * mm});
            skLineSegment(sketch, "E191.top", {"start": v(-34, 11) * mm, "end": v(-35, 11) * mm});
            skLineSegment(sketch, "E191.left", {"start": v(-34, 11.5) * mm, "end": v(-34, 11) * mm});
            skLineSegment(sketch, "E191.right", {"start": v(-35, 11.5) * mm, "end": v(-35, 11) * mm});
            skLineSegment(sketch, "E192.MirrorCS", {"start": v(-35, 23.5) * mm, "end": v(-35, 24) * mm});
            skLineSegment(sketch, "E193.MirrorCS", {"start": v(-34, 23.5) * mm, "end": v(-34, 24) * mm});
            skLineSegment(sketch, "E194.MirrorCS", {"start": v(-27, 23.5) * mm, "end": v(-27, 24) * mm});
            skLineSegment(sketch, "E195.MirrorCS", {"start": v(-28, 23.5) * mm, "end": v(-28, 24) * mm});
            skLineSegment(sketch, "E196.MirrorCS", {"start": v(-34, 24) * mm, "end": v(-35, 24) * mm});
            skLineSegment(sketch, "E197.MirrorCS", {"start": v(-27, 23.5) * mm, "end": v(-28, 23.5) * mm});
            skLineSegment(sketch, "E198.MirrorCS", {"start": v(-27, 24) * mm, "end": v(-28, 24) * mm});
            skLineSegment(sketch, "E199.MirrorCS", {"start": v(-34, 23.5) * mm, "end": v(-35, 23.5) * mm});
            skLineSegment(sketch, "E200", {"start": v(42.5, 36.25) * mm, "end": v(-42.5, 36.25) * mm, "construction": true});
            skLineSegment(sketch, "E201.bottom", {"start": v(-29.2, 28.75) * mm, "end": v(-30.2, 28.75) * mm});
            skLineSegment(sketch, "E201.top", {"start": v(-29.2, 28.25) * mm, "end": v(-30.2, 28.25) * mm});
            skLineSegment(sketch, "E201.left", {"start": v(-29.2, 28.75) * mm, "end": v(-29.2, 28.25) * mm});
            skLineSegment(sketch, "E201.right", {"start": v(-30.2, 28.75) * mm, "end": v(-30.2, 28.25) * mm});
            skLineSegment(sketch, "E202.MirrorCS", {"start": v(-29.2, 43.75) * mm, "end": v(-29.2, 44.25) * mm});
            skLineSegment(sketch, "E203.MirrorCS", {"start": v(-30.2, 43.75) * mm, "end": v(-30.2, 44.25) * mm});
            skLineSegment(sketch, "E204.MirrorCS", {"start": v(-29.2, 43.75) * mm, "end": v(-30.2, 43.75) * mm});
            skLineSegment(sketch, "E205.MirrorCS", {"start": v(-29.2, 44.25) * mm, "end": v(-30.2, 44.25) * mm});
            skLineSegment(sketch, "E206.bottom", {"start": v(39.5, 8.1) * mm, "end": v(36.5, 8.1) * mm});
            skLineSegment(sketch, "E206.top", {"start": v(39.5, 8.6) * mm, "end": v(36.5, 8.6) * mm});
            skLineSegment(sketch, "E206.left", {"start": v(39.5, 8.1) * mm, "end": v(39.5, 8.6) * mm});
            skLineSegment(sketch, "E206.right", {"start": v(36.5, 8.1) * mm, "end": v(36.5, 8.6) * mm});
            skLineSegment(sketch, "E207.MirrorCS", {"start": v(36.5, 28.9) * mm, "end": v(36.5, 28.4) * mm});
            skLineSegment(sketch, "E208.MirrorCS", {"start": v(39.5, 28.9) * mm, "end": v(39.5, 28.4) * mm});
            skLineSegment(sketch, "E209.MirrorCS", {"start": v(39.5, 28.4) * mm, "end": v(36.5, 28.4) * mm});
            skLineSegment(sketch, "E210.MirrorCS", {"start": v(39.5, 28.9) * mm, "end": v(36.5, 28.9) * mm});
            skLineSegment(sketch, "E211", {"start": v(42.5, 35) * mm, "end": v(-42.5, 35) * mm, "construction": true});
            skLineSegment(sketch, "E212.bottom", {"start": v(-1, 25.1) * mm, "end": v(-4, 25.1) * mm});
            skLineSegment(sketch, "E212.top", {"start": v(-1, 24.6) * mm, "end": v(-4, 24.6) * mm});
            skLineSegment(sketch, "E212.left", {"start": v(-1, 25.1) * mm, "end": v(-1, 24.6) * mm});
            skLineSegment(sketch, "E212.right", {"start": v(-4, 25.1) * mm, "end": v(-4, 24.6) * mm});
            skLineSegment(sketch, "E213.MirrorCS", {"start": v(-4, 44.9) * mm, "end": v(-4, 45.4) * mm});
            skLineSegment(sketch, "E214.MirrorCS", {"start": v(-1, 44.9) * mm, "end": v(-1, 45.4) * mm});
            skLineSegment(sketch, "E215.MirrorCS", {"start": v(-1, 45.4) * mm, "end": v(-4, 45.4) * mm});
            skLineSegment(sketch, "E216.MirrorCS", {"start": v(-1, 44.9) * mm, "end": v(-4, 44.9) * mm});
            skLineSegment(sketch, "E217.bottom", {"start": v(28.1, 48) * mm, "end": v(35.7, 48) * mm});
            skLineSegment(sketch, "E217.top", {"start": v(28.1, 42.4) * mm, "end": v(35.7, 42.4) * mm});
            skLineSegment(sketch, "E217.left", {"start": v(28.1, 48) * mm, "end": v(28.1, 42.4) * mm});
            skLineSegment(sketch, "E217.right", {"start": v(35.7, 48) * mm, "end": v(35.7, 42.4) * mm});
            skLineSegment(sketch, "E218.bottom", {"start": v(29.4, 45.5) * mm, "end": v(30.03, 45.5) * mm});
            skLineSegment(sketch, "E218.top", {"start": v(29.4, 43.5) * mm, "end": v(30.03, 43.5) * mm});
            skLineSegment(sketch, "E218.left", {"start": v(29.4, 45.5) * mm, "end": v(29.4, 43.5) * mm});
            skLineSegment(sketch, "E218.right", {"start": v(30.03, 45.5) * mm, "end": v(30.03, 43.5) * mm});
            skLineSegment(sketch, "E219.bottom", {"start": v(34.03, 45.5) * mm, "end": v(34.4, 45.5) * mm});
            skLineSegment(sketch, "E219.top", {"start": v(34.03, 43.5) * mm, "end": v(34.4, 43.5) * mm});
            skLineSegment(sketch, "E219.left", {"start": v(34.03, 45.5) * mm, "end": v(34.03, 43.5) * mm});
            skLineSegment(sketch, "E219.right", {"start": v(34.4, 45.5) * mm, "end": v(34.4, 43.5) * mm});
            skLineSegment(sketch, "E220.bottom", {"start": v(3, 48.5) * mm, "end": v(18, 48.5) * mm});
            skLineSegment(sketch, "E220.top", {"start": v(3, 38) * mm, "end": v(18, 38) * mm});
            skLineSegment(sketch, "E220.left", {"start": v(3, 48.5) * mm, "end": v(3, 38) * mm});
            skLineSegment(sketch, "E220.right", {"start": v(18, 48.5) * mm, "end": v(18, 38) * mm});
            skLineSegment(sketch, "E221.left", {"start": v(3, 44) * mm, "end": v(3, 38) * mm});
            skLineSegment(sketch, "E221.right", {"start": v(3.5, 44) * mm, "end": v(3.5, 38) * mm});
            skLineSegment(sketch, "E222.bottom", {"start": v(17.5, 44) * mm, "end": v(18, 44) * mm});
            skLineSegment(sketch, "E222.top", {"start": v(17.5, 38) * mm, "end": v(18, 38) * mm});
            skLineSegment(sketch, "E222.left", {"start": v(17.5, 44) * mm, "end": v(17.5, 38) * mm});
            skLineSegment(sketch, "E222.right", {"start": v(18, 44) * mm, "end": v(18, 38) * mm});
            skPoint(sketch, "E223", {"position": v(3, 48.5) * mm});
            skLineSegment(sketch, "E224.left", {"start": v(-14.5, 45) * mm, "end": v(-14.5, 44) * mm});
            skLineSegment(sketch, "E224.right", {"start": v(-14, 45) * mm, "end": v(-14, 44) * mm});
            skLineSegment(sketch, "E225.bottom", {"start": v(-16.4, 64.56) * mm, "end": v(-15.9, 64.56) * mm});
            skLineSegment(sketch, "E225.top", {"start": v(-16.4, 63.56) * mm, "end": v(-15.9, 63.56) * mm});
            skLineSegment(sketch, "E225.left", {"start": v(-16.4, 64.56) * mm, "end": v(-16.4, 63.56) * mm});
            skLineSegment(sketch, "E225.right", {"start": v(-15.9, 64.56) * mm, "end": v(-15.9, 63.56) * mm});
            skLineSegment(sketch, "E226.bottom", {"start": v(-9.4, 35) * mm, "end": v(-8, 35) * mm});
            skLineSegment(sketch, "E226.top", {"start": v(-9.4, 34) * mm, "end": v(-8, 34) * mm});
            skLineSegment(sketch, "E226.left", {"start": v(-8, 35) * mm, "end": v(-8, 34) * mm});
            skLineSegment(sketch, "E226.right", {"start": v(-9.4, 35) * mm, "end": v(-9.4, 34) * mm});
            skLineSegment(sketch, "E227.bottom", {"start": v(-8, 45) * mm, "end": v(-7.5, 45) * mm});
            skLineSegment(sketch, "E227.top", {"start": v(-8, 44) * mm, "end": v(-7.5, 44) * mm});
            skLineSegment(sketch, "E227.left", {"start": v(-8, 45) * mm, "end": v(-8, 44) * mm});
            skLineSegment(sketch, "E227.right", {"start": v(-7.5, 45) * mm, "end": v(-7.5, 44) * mm});
            skLineSegment(sketch, "E228.top", {"start": v(-14.5, 46.5) * mm, "end": v(-8, 46.5) * mm});
            skLineSegment(sketch, "E229.bottom", {"start": v(-14.5, 46.5) * mm, "end": v(-7.5, 46.5) * mm});
            skLineSegment(sketch, "E229.top", {"start": v(-14.5, 34) * mm, "end": v(-7.5, 34) * mm});
            skLineSegment(sketch, "E229.left", {"start": v(-14.5, 46.5) * mm, "end": v(-14.5, 34) * mm});
            skLineSegment(sketch, "E229.right", {"start": v(-7.5, 46.5) * mm, "end": v(-7.5, 34) * mm});
            skLineSegment(sketch, "E230.bottom", {"start": v(-8, 46.5) * mm, "end": v(-14, 46.5) * mm});
            skLineSegment(sketch, "E230.top", {"start": v(-8, 49) * mm, "end": v(-14, 49) * mm});
            skLineSegment(sketch, "E230.left", {"start": v(-8, 46.5) * mm, "end": v(-8, 49) * mm});
            skLineSegment(sketch, "E230.right", {"start": v(-14, 46.5) * mm, "end": v(-14, 49) * mm});
            skSolve(sketch);
        }
        {
            var Q0;
            {var subQ10=sQuery(id+"F0.wireOp",EDGE,"E2");var subQ12=sQuery(id+"F0.wireOp",EDGE,"E0.7");Q0=makeQuery(id+"FgA4i82gOfAXOqg_2.opBoolean","SPLIT",FACE,{"disambiguationData":[TD([makeQuery(id+"F1.opExtrude","SWEPT_FACE",FACE,{"disambiguationData":[OSD([subQ10])]})])],"derivedFrom":makeQuery(id+"F1.opExtrude","SWEPT_FACE",FACE,{"disambiguationData":[OSD([subQ12])]})});}
            var sketch = newSketch(context, id + "F9", { "sketchPlane" : qUnion([Q0])});
            skCircle(sketch, "E231", {"center": v(39, -6) * mm, "radius": 1.68 * mm});
            skCircle(sketch, "E232.0", {"center": v(39, -6) * mm, "radius": 3.68 * mm});
            skCircle(sketch, "E233", {"center": v(-19, -6) * mm, "radius": 1.68 * mm});
            skCircle(sketch, "E234", {"center": v(-19, 43) * mm, "radius": 1.68 * mm});
            skCircle(sketch, "E235", {"center": v(39, 43) * mm, "radius": 1.68 * mm});
            skCircle(sketch, "E236.0", {"center": v(-19, -6) * mm, "radius": 3.68 * mm});
            skCircle(sketch, "E237.0", {"center": v(-19, 43) * mm, "radius": 3.68 * mm});
            skCircle(sketch, "E238.0", {"center": v(39, 43) * mm, "radius": 3.68 * mm});
            skSolve(sketch);
        }
        {
            var Q0;
            Q0 = qSketchRegion(id + "F9", true);
            var Q1;
            Q1=makeQuery(id+"F9.imprint","IMPRINT",FACE,{"disambiguationData":[TD([[makeQuery(id+"F9.imprint","IMPRINT",EDGE,{"derivedFrom":sQuery(id+"F9.wireOp",EDGE,"E234")}),1.0]])]});
            var Q2;
            Q2=makeQuery(id+"F9.imprint","IMPRINT",FACE,{"disambiguationData":[TD([[makeQuery(id+"F9.imprint","IMPRINT",EDGE,{"derivedFrom":sQuery(id+"F9.wireOp",EDGE,"E235")}),1.0]])]});
            var Q3;
            {var subQ0=sQuery(id+"F9.wireOp",EDGE,"E231");var subQ1=sQuery(id+"FVGj8xa2IfCb6cx_3.wireOp",EDGE,"532f86e5-7fd5-457e-af95-5528fb01fa4e");var subQ2=makeQuery(id+"FVGj8xa2IfCb6cx_3.imprint","IMPRINT",EDGE,{"disambiguationData":[TD([[makeQuery(id+"FVGj8xa2IfCb6cx_3.imprint","INTERSECT",VERTEX,{"derivedFrom":[sQuery(id+"FVGj8xa2IfCb6cx_3.wireOp",EDGE,"4a2102cf-7dbc-4f38-9e27-ae855fa31068"),subQ1]}),-1.0]])],"derivedFrom":subQ1});var subQ3=makeQuery(id+"F9.imprint","INTERSECT",VERTEX,{"disambiguationData":[OD(0.0)],"derivedFrom":[subQ2,subQ0]});Q3=makeQuery(id+"F9.imprint","IMPRINT",FACE,{"disambiguationData":[TD([[makeQuery(id+"F9.imprint","IMPRINT",EDGE,{"disambiguationData":[TD([[subQ3,-1.0]])],"derivedFrom":subQ0}),1.0]])]});}
            var Q4;
            {var subQ0=sQuery(id+"F9.wireOp",EDGE,"E231");var subQ1=sQuery(id+"FVGj8xa2IfCb6cx_3.wireOp",EDGE,"532f86e5-7fd5-457e-af95-5528fb01fa4e");var subQ2=makeQuery(id+"FVGj8xa2IfCb6cx_3.imprint","IMPRINT",EDGE,{"disambiguationData":[TD([[makeQuery(id+"FVGj8xa2IfCb6cx_3.imprint","INTERSECT",VERTEX,{"derivedFrom":[sQuery(id+"FVGj8xa2IfCb6cx_3.wireOp",EDGE,"4a2102cf-7dbc-4f38-9e27-ae855fa31068"),subQ1]}),-1.0]])],"derivedFrom":subQ1});var subQ3=makeQuery(id+"F9.imprint","INTERSECT",VERTEX,{"disambiguationData":[OD(0.0)],"derivedFrom":[subQ2,subQ0]});Q4=makeQuery(id+"F9.imprint","IMPRINT",FACE,{"disambiguationData":[TD([[makeQuery(id+"F9.imprint","IMPRINT",EDGE,{"disambiguationData":[TD([[subQ3,1.0]])],"derivedFrom":subQ0}),1.0]])]});}
            var Q5;
            Q5=makeQuery(id+"F9.imprint","IMPRINT",FACE,{"disambiguationData":[TD([[makeQuery(id+"F9.imprint","IMPRINT",EDGE,{"derivedFrom":sQuery(id+"F9.wireOp",EDGE,"E233")}),1.0]])]});
            extrude(context, id + "F10", {"entities" : qUnion([Q0, Q1, Q2, Q3, Q4, Q5]), "operationType" : NewBodyOperationType.ADD, "depth" : 11 * mm, "offsetDistance" : 25 * mm});
        }
        {
            var Q0;
            Q0=makeQuery(id+"F10.opExtrude","CAP_FACE",FACE,{"disambiguationData":[OSD([sQuery(id+"F9.wireOp",EDGE,"E237.0")])],"isStart":false});
            var sketch = newSketch(context, id + "F11", { "sketchPlane" : qUnion([Q0])});
            skPoint(sketch, "E239", {"position": v(-19, 43) * mm});
            skPoint(sketch, "E240", {"position": v(39, 43) * mm});
            skPoint(sketch, "E241", {"position": v(39, -6) * mm});
            skPoint(sketch, "E242", {"position": v(-19, -6) * mm});
            skCircle(sketch, "E243", {"center": v(-19, 43) * mm, "radius": 1.68 * mm});
            skCircle(sketch, "E244", {"center": v(39, 43) * mm, "radius": 1.68 * mm});
            skCircle(sketch, "E245", {"center": v(39, -6) * mm, "radius": 1.68 * mm});
            skCircle(sketch, "E246", {"center": v(-19, -6) * mm, "radius": 1.68 * mm});
            skSolve(sketch);
        }
        {
            var Q0;
            Q0 = qSketchRegion(id + "F11", true);
            extrude(context, id + "F12", {"entities" : qUnion([Q0]), "operationType" : NewBodyOperationType.REMOVE, "oppositeDirection" : true, "depth" : 6 * mm, "offsetDistance" : 25 * mm});
        }
        {
            var Q0;
            Q0=makeQuery(id+"F7.opPattern","COPY",FACE,{"derivedFrom":makeQuery(id+"F6.opExtrude","CAP_FACE",FACE,{"disambiguationData":[OSD([sQuery(id+"F5.wireOp",EDGE,"E13.0"),sQuery(id+"F5.wireOp",EDGE,"E13.1"),sQuery(id+"F5.wireOp",EDGE,"E13.2"),sQuery(id+"F5.wireOp",EDGE,"E13.3"),sQuery(id+"F5.wireOp",EDGE,"E13.4"),sQuery(id+"F5.wireOp",EDGE,"E13.5"),sQuery(id+"F5.wireOp",EDGE,"E14.bottom"),sQuery(id+"F5.wireOp",EDGE,"E14.top"),sQuery(id+"F5.wireOp",EDGE,"E14.left"),sQuery(id+"F5.wireOp",EDGE,"E14.right")])],"isStart":false}),"instanceName":"1"});
            var sketch = newSketch(context, id + "F13", { "sketchPlane" : qUnion([Q0])});
            skPoint(sketch, "E247", {"position": v(0, 10.17) * mm});
            skCircle(sketch, "E248.cCircle", {"center": v(0, 10.17) * mm, "radius": 2.92 * mm, "construction": true});
            skLineSegment(sketch, "E248.0", {"start": v(3.37, 10.17) * mm, "end": v(1.69, 7.25) * mm});
            skLineSegment(sketch, "E248.1", {"start": v(1.69, 7.25) * mm, "end": v(-1.69, 7.25) * mm});
            skLineSegment(sketch, "E248.2", {"start": v(-1.69, 7.25) * mm, "end": v(-3.38, 10.17) * mm});
            skLineSegment(sketch, "E248.3", {"start": v(-3.37, 10.17) * mm, "end": v(-1.69, 13.1) * mm});
            skLineSegment(sketch, "E248.4", {"start": v(-1.69, 13.1) * mm, "end": v(1.69, 13.1) * mm});
            skLineSegment(sketch, "E248.5", {"start": v(1.69, 13.1) * mm, "end": v(3.38, 10.17) * mm});
            skPoint(sketch, "E248.0.midPoint", {"position": v(2.53, 8.7) * mm});
            skSolve(sketch);
        }
        {
            var Q0;
            Q0 = qSketchRegion(id + "F13", true);
            extrude(context, id + "F14", {"entities" : qUnion([Q0]), "operationType" : NewBodyOperationType.REMOVE, "oppositeDirection" : true, "depth" : 2 * mm, "offsetDistance" : 25 * mm});
        }
    });
